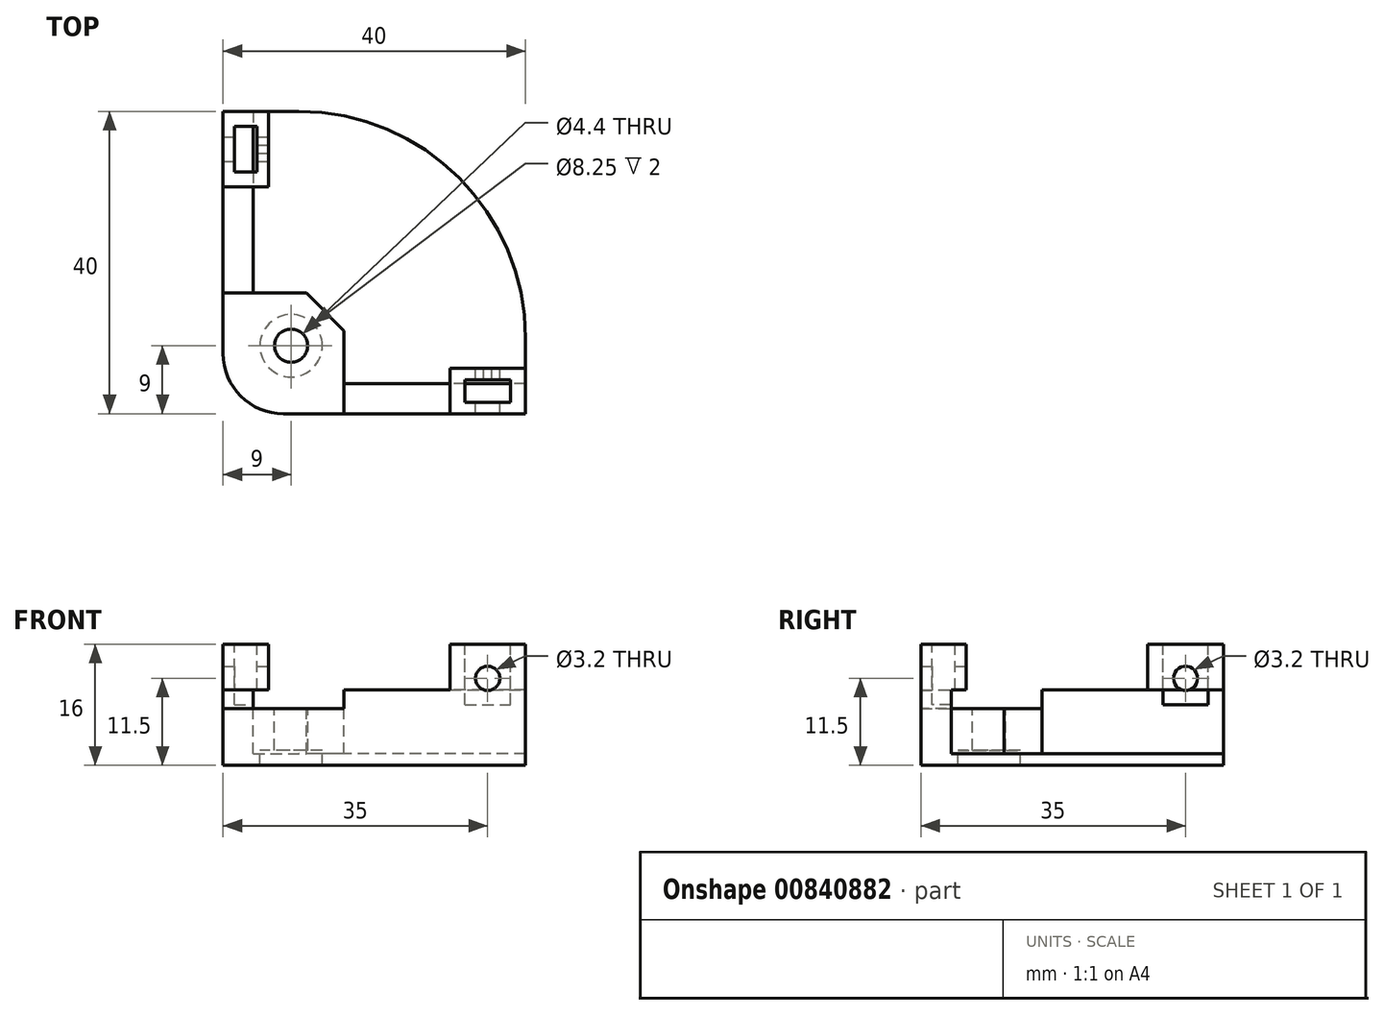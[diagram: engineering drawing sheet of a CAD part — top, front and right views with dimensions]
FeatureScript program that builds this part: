
annotation { "Feature Type Name" : "Feature", "Feature Type Description" : "" }
export const myFeature = defineFeature(function(context is Context, id is Id, definition is map)
    precondition{}
    {
        {
            var Q0;
            Q0=qCreatedBy(makeId("Top.planeOp"),FACE);
            var sketch = newSketch(context, id + "F0", { "sketchPlane" : qUnion([Q0])});
            skLineSegment(sketch, "E0.bottom", {"start": v(0, 0) * mm, "end": v(40, 0) * mm});
            skLineSegment(sketch, "E0.top", {"start": v(0, 40) * mm, "end": v(40, 40) * mm});
            skLineSegment(sketch, "E0.left", {"start": v(0, 0) * mm, "end": v(0, 40) * mm});
            skLineSegment(sketch, "E0.right", {"start": v(40, 0) * mm, "end": v(40, 40) * mm});
            skSolve(sketch);
        }
        {
            var Q0;
            Q0=qSketchRegion(id+"F0",true);
            extrude(context, id + "F1", {"entities" : qUnion([Q0]), "depth" : 10 * mm, "offsetDistance" : 25 * mm});
        }
        {
            var Q0;
            Q0=makeQuery(id+"F1.opExtrude","CAP_FACE",FACE,{"disambiguationData":[OSD([sQuery(id+"F0.wireOp",EDGE,"E0.bottom"),sQuery(id+"F0.wireOp",EDGE,"E0.top"),sQuery(id+"F0.wireOp",EDGE,"E0.left"),sQuery(id+"F0.wireOp",EDGE,"E0.right")])],"isStart":false});
            var sketch = newSketch(context, id + "F2", { "sketchPlane" : qUnion([Q0])});
            skLineSegment(sketch, "E1.bottom", {"start": v(40, 40) * mm, "end": v(4, 40) * mm});
            skLineSegment(sketch, "E1.top", {"start": v(40, 4) * mm, "end": v(16, 4) * mm});
            skLineSegment(sketch, "E1.left", {"start": v(40, 40) * mm, "end": v(40, 4) * mm});
            skLineSegment(sketch, "E1.right", {"start": v(4, 40) * mm, "end": v(4, 16) * mm});
            skLineSegment(sketch, "E2", {"start": v(4, 16) * mm, "end": v(11, 16) * mm});
            skLineSegment(sketch, "E3", {"start": v(16, 11) * mm, "end": v(16, 4) * mm});
            skLineSegment(sketch, "E4", {"start": v(16, 11) * mm, "end": v(11, 16) * mm});
            skPoint(sketch, "E5.orphan", {"position": v(16, 16) * mm});
            skSolve(sketch);
        }
        {
            var Q0;
            Q0=qSketchRegion(id+"F2",true);
            extrude(context, id + "F3", {"entities" : qUnion([Q0]), "operationType" : NewBodyOperationType.REMOVE, "oppositeDirection" : true, "depth" : 8.5 * mm, "offsetDistance" : 25 * mm});
        }
        {
            var Q0;
            Q0=makeQuery(id+"F1.opExtrude","CAP_FACE",FACE,{"disambiguationData":[OSD([sQuery(id+"F0.wireOp",EDGE,"E0.bottom"),sQuery(id+"F0.wireOp",EDGE,"E0.top"),sQuery(id+"F0.wireOp",EDGE,"E0.left"),sQuery(id+"F0.wireOp",EDGE,"E0.right")])],"isStart":false});
            var sketch = newSketch(context, id + "F4", { "sketchPlane" : qUnion([Q0])});
            skLineSegment(sketch, "E6.bottom", {"start": v(0, 0) * mm, "end": v(16, 0) * mm});
            skLineSegment(sketch, "E6.top", {"start": v(0, 16) * mm, "end": v(16, 16) * mm});
            skLineSegment(sketch, "E6.left", {"start": v(0, 0) * mm, "end": v(0, 16) * mm});
            skLineSegment(sketch, "E6.right", {"start": v(16, 0) * mm, "end": v(16, 16) * mm});
            skSolve(sketch);
        }
        {
            var Q0;
            Q0=qSketchRegion(id+"F4",true);
            extrude(context, id + "F5", {"entities" : qUnion([Q0]), "operationType" : NewBodyOperationType.REMOVE, "oppositeDirection" : true, "depth" : 2.5 * mm, "offsetDistance" : 25 * mm});
        }
        {
            var Q0;
            Q0=makeQuery(id+"F1.opExtrude","CAP_FACE",FACE,{"disambiguationData":[OSD([sQuery(id+"F0.wireOp",EDGE,"E0.bottom"),sQuery(id+"F0.wireOp",EDGE,"E0.top"),sQuery(id+"F0.wireOp",EDGE,"E0.left"),sQuery(id+"F0.wireOp",EDGE,"E0.right")])],"isStart":true});
            var sketch = newSketch(context, id + "F6", { "sketchPlane" : qUnion([Q0])});
            skPoint(sketch, "E7", {"position": v(9, -9) * mm});
            skSolve(sketch);
        }
        {
            var Q0;
            Q0=sQuery(id+"F6.wireOp",VERTEX,"E7");
            var Q1;
            Q1=makeQuery(id+"F1.opExtrude","SWEPT_BODY",BODY,{"disambiguationData":[OSD([sQuery(id+"F0.wireOp",EDGE,"E0.bottom"),sQuery(id+"F0.wireOp",EDGE,"E0.top"),sQuery(id+"F0.wireOp",EDGE,"E0.left"),sQuery(id+"F0.wireOp",EDGE,"E0.right")])]});
            hole(context, id + "F7", {"style" : HoleStyle.C_BORE, "endStyle" : HoleEndStyle.THROUGH, "holeDiameter" : 4.4 * mm, "cBoreDiameter" : 8.25 * mm, "cBoreDepth" : 2 * mm, "majorDiameter" : 5 * mm, "isTappedThrough" : true, "tappedDepth" : 12 * mm, "tapClearance" : 3, "locations" : qUnion([Q0]), "scope" : qUnion([Q1])});
        }
        {
            var Q0;
            {var subQ0=sQuery(id+"F0.wireOp",EDGE,"E0.top");var subQ1=sQuery(id+"F0.wireOp",EDGE,"E0.left");Q0=makeQuery(id+"F5.boolean.opBoolean","SPLIT",FACE,{"disambiguationData":[TD([makeQuery(id+"F1.opExtrude","SWEPT_FACE",FACE,{"disambiguationData":[OSD([subQ0])]})])],"derivedFrom":makeQuery(id+"F1.opExtrude","CAP_FACE",FACE,{"disambiguationData":[OSD([sQuery(id+"F0.wireOp",EDGE,"E0.bottom"),subQ0,subQ1,sQuery(id+"F0.wireOp",EDGE,"E0.right")])],"isStart":false})});}
            var sketch = newSketch(context, id + "F8", { "sketchPlane" : qUnion([Q0])});
            skLineSegment(sketch, "E8.bottom", {"start": v(0, 40) * mm, "end": v(6, 40) * mm});
            skLineSegment(sketch, "E8.top", {"start": v(0, 30) * mm, "end": v(6, 30) * mm});
            skLineSegment(sketch, "E8.left", {"start": v(0, 40) * mm, "end": v(0, 30) * mm});
            skLineSegment(sketch, "E8.right", {"start": v(6, 40) * mm, "end": v(6, 30) * mm});
            skLineSegment(sketch, "E9.bottom", {"start": v(40, 0) * mm, "end": v(30, 0) * mm});
            skLineSegment(sketch, "E9.top", {"start": v(40, 6) * mm, "end": v(30, 6) * mm});
            skLineSegment(sketch, "E9.left", {"start": v(40, 0) * mm, "end": v(40, 6) * mm});
            skLineSegment(sketch, "E9.right", {"start": v(30, 0) * mm, "end": v(30, 6) * mm});
            skSolve(sketch);
        }
        {
            var Q0;
            Q0=qSketchRegion(id+"F8",true);
            extrude(context, id + "F9", {"entities" : qUnion([Q0]), "operationType" : NewBodyOperationType.ADD, "depth" : 6 * mm, "offsetDistance" : 25 * mm});
        }
        {
            var Q0;
            Q0=makeQuery(id+"F1.opExtrude","SWEPT_FACE",FACE,{"disambiguationData":[OSD([sQuery(id+"F0.wireOp",EDGE,"E0.left")])]});
            var sketch = newSketch(context, id + "F10", { "sketchPlane" : qUnion([Q0])});
            skPoint(sketch, "E10", {"position": v(-35, 11.5) * mm});
            skSolve(sketch);
        }
        {
            var Q0;
            Q0=sQuery(id+"F10.wireOp",VERTEX,"E10");
            var Q1;
            Q1=makeQuery(id+"F1.opExtrude","SWEPT_BODY",BODY,{"disambiguationData":[OSD([sQuery(id+"F0.wireOp",EDGE,"E0.bottom"),sQuery(id+"F0.wireOp",EDGE,"E0.top"),sQuery(id+"F0.wireOp",EDGE,"E0.left"),sQuery(id+"F0.wireOp",EDGE,"E0.right")])]});
            hole(context, id + "F11", {"style" : HoleStyle.SIMPLE, "endStyle" : HoleEndStyle.THROUGH, "holeDiameter" : 3.2 * mm, "majorDiameter" : 5 * mm, "isTappedThrough" : true, "tappedDepth" : 12 * mm, "tapClearance" : 3, "locations" : qUnion([Q0]), "scope" : qUnion([Q1])});
        }
        {
            var Q0;
            Q0=makeQuery(id+"F9.opExtrude","CAP_FACE",FACE,{"disambiguationData":[OSD([sQuery(id+"F8.wireOp",EDGE,"E8.bottom"),sQuery(id+"F8.wireOp",EDGE,"E8.top"),sQuery(id+"F8.wireOp",EDGE,"E8.left"),sQuery(id+"F8.wireOp",EDGE,"E8.right")])],"isStart":false});
            var sketch = newSketch(context, id + "F12", { "sketchPlane" : qUnion([Q0])});
            skLineSegment(sketch, "E11.bottom", {"start": v(1.5, 38) * mm, "end": v(4.5, 38) * mm});
            skLineSegment(sketch, "E11.top", {"start": v(1.5, 32) * mm, "end": v(4.5, 32) * mm});
            skLineSegment(sketch, "E11.left", {"start": v(1.5, 38) * mm, "end": v(1.5, 32) * mm});
            skLineSegment(sketch, "E11.right", {"start": v(4.5, 38) * mm, "end": v(4.5, 32) * mm});
            skLineSegment(sketch, "E12.bottom", {"start": v(38, 4.5) * mm, "end": v(32, 4.5) * mm});
            skLineSegment(sketch, "E12.top", {"start": v(38, 1.5) * mm, "end": v(32, 1.5) * mm});
            skLineSegment(sketch, "E12.left", {"start": v(38, 4.5) * mm, "end": v(38, 1.5) * mm});
            skLineSegment(sketch, "E12.right", {"start": v(32, 4.5) * mm, "end": v(32, 1.5) * mm});
            skSolve(sketch);
        }
        {
            var Q0;
            Q0=qSketchRegion(id+"F12",true);
            extrude(context, id + "F13", {"entities" : qUnion([Q0]), "operationType" : NewBodyOperationType.REMOVE, "oppositeDirection" : true, "depth" : 8 * mm, "offsetDistance" : 25 * mm});
        }
        {
            var Q0;
            Q0=makeQuery(id+"F9.boolean.opBoolean","MERGE",FACE,{"derivedFrom":[makeQuery(id+"F1.opExtrude","SWEPT_FACE",FACE,{"disambiguationData":[OSD([sQuery(id+"F0.wireOp",EDGE,"E0.bottom")])]}),makeQuery(id+"F9.opExtrude","SWEPT_FACE",FACE,{"disambiguationData":[OSD([sQuery(id+"F8.wireOp",EDGE,"E9.bottom")])]})]});
            var sketch = newSketch(context, id + "F14", { "sketchPlane" : qUnion([Q0])});
            skPoint(sketch, "E13", {"position": v(35, 11.5) * mm});
            skSolve(sketch);
        }
        {
            var Q0;
            Q0=sQuery(id+"F14.wireOp",VERTEX,"E13");
            var Q1;
            Q1=makeQuery(id+"F1.opExtrude","SWEPT_BODY",BODY,{"disambiguationData":[OSD([sQuery(id+"F0.wireOp",EDGE,"E0.bottom"),sQuery(id+"F0.wireOp",EDGE,"E0.top"),sQuery(id+"F0.wireOp",EDGE,"E0.left"),sQuery(id+"F0.wireOp",EDGE,"E0.right")])]});
            hole(context, id + "F15", {"style" : HoleStyle.SIMPLE, "endStyle" : HoleEndStyle.THROUGH, "holeDiameter" : 3.2 * mm, "majorDiameter" : 5 * mm, "isTappedThrough" : true, "tappedDepth" : 12 * mm, "tapClearance" : 3, "locations" : qUnion([Q0]), "scope" : qUnion([Q1])});
        }
        {
            var Q0;
            Q0=makeQuery(id+"F1.opExtrude","SWEPT_EDGE",EDGE,{"disambiguationData":[OSD([sQuery(id+"F0.wireOp",EDGE,"E0.top"),sQuery(id+"F0.wireOp",EDGE,"E0.right")])]});
            fillet(context, id + "F16", {"entities" : qUnion([Q0]), "radius" : 30 * mm, "tangentPropagation" : true, "allowEdgeOverflow" : false});
        }
        {
            var Q0;
            Q0=makeQuery(id+"F1.opExtrude","SWEPT_EDGE",EDGE,{"disambiguationData":[OSD([sQuery(id+"F0.wireOp",EDGE,"E0.bottom"),sQuery(id+"F0.wireOp",EDGE,"E0.left")])]});
            fillet(context, id + "F17", {"entities" : qUnion([Q0]), "radius" : 8 * mm, "tangentPropagation" : true, "allowEdgeOverflow" : false});
        }
    });
